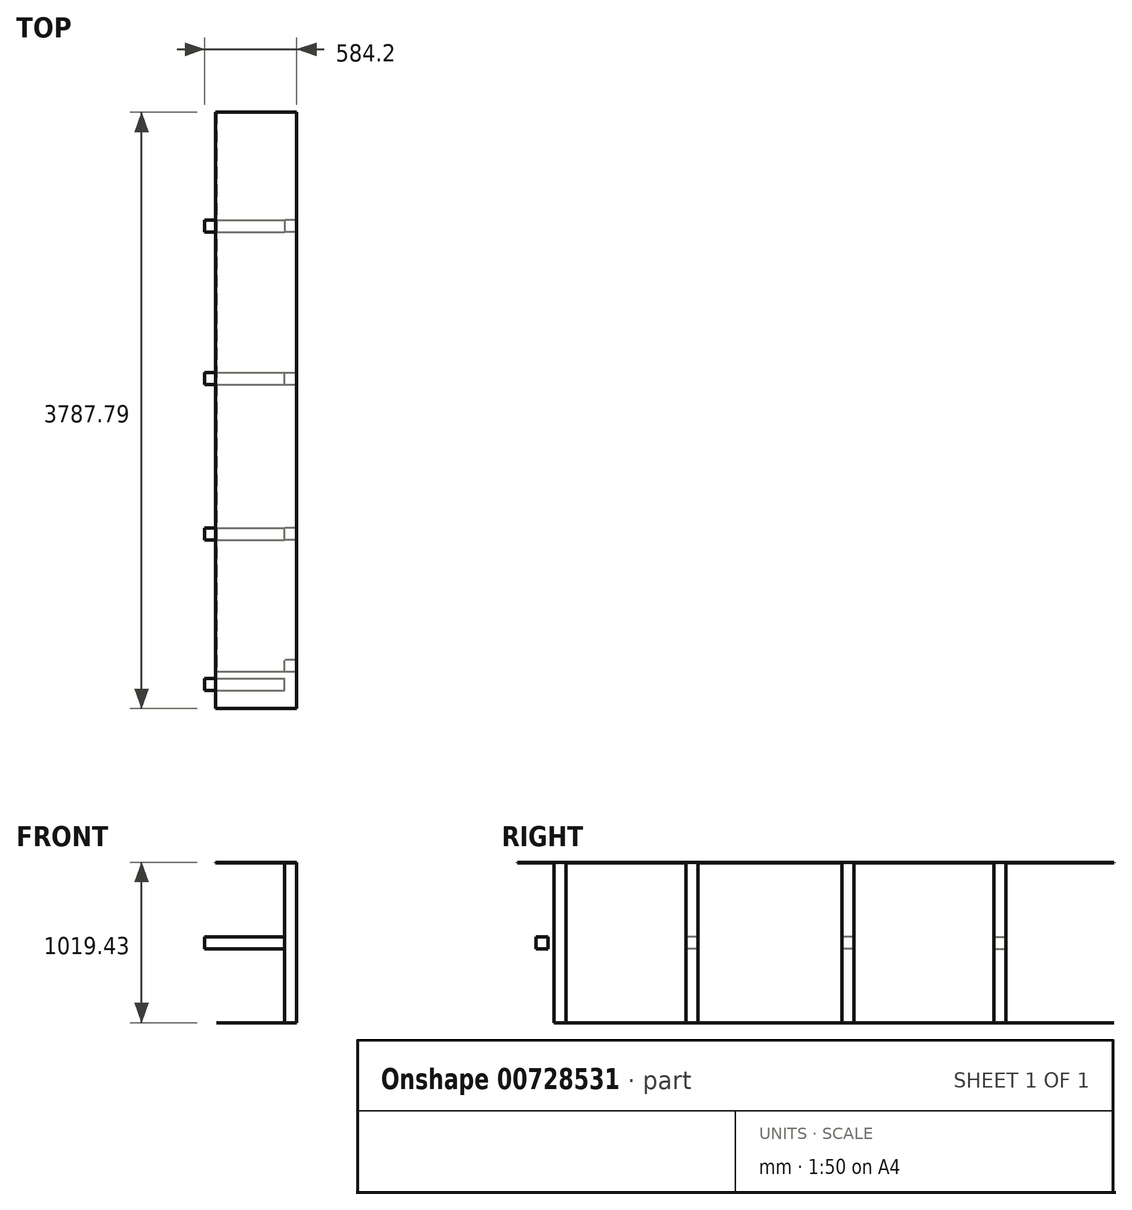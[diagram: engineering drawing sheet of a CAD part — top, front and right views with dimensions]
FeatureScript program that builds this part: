
annotation { "Feature Type Name" : "Feature", "Feature Type Description" : "" }
export const myFeature = defineFeature(function(context is Context, id is Id, definition is map)
    precondition{}
    {
        {
            var Q0;
            Q0=qCreatedBy(makeId("Top.planeOp"),FACE);
            var sketch = newSketch(context, id + "F0", { "sketchPlane" : qUnion([Q0])});
            skLineSegment(sketch, "E0.bottom", {"start": v(254, 1854.2) * mm, "end": v(-254, 1854.2) * mm});
            skLineSegment(sketch, "E0.top", {"start": v(254, -1854.2) * mm, "end": v(-254, -1854.2) * mm});
            skLineSegment(sketch, "E0.left", {"start": v(254, 1854.2) * mm, "end": v(254, -1854.2) * mm});
            skLineSegment(sketch, "E0.right", {"start": v(-254, 1854.2) * mm, "end": v(-254, -1854.2) * mm});
            skPoint(sketch, "E0.middle", {"position": v(0, 0) * mm});
            skLineSegment(sketch, "E1.bottom", {"start": v(254, 1854.2) * mm, "end": v(162.05, 1854.2) * mm});
            skLineSegment(sketch, "E1.left", {"start": v(254, 1854.2) * mm, "end": v(254, 1760.58) * mm});
            skLineSegment(sketch, "E1.right", {"start": v(162.05, 2217.78) * mm, "end": v(162.05, 1854.2) * mm});
            skPoint(sketch, "E2.oppositeSnap0", {"position": v(162.05, 2036) * mm});
            skLineSegment(sketch, "E2.bottom", {"start": v(254, -1854.2) * mm, "end": v(162.05, -1854.2) * mm});
            skLineSegment(sketch, "E2.left", {"start": v(254, -1854.2) * mm, "end": v(254, -1764.17) * mm});
            skLineSegment(sketch, "E2.right", {"start": v(162.05, -1854.2) * mm, "end": v(162.05, -1764.17) * mm});
            skSolve(sketch);
        }
        {
            var Q0;
            Q0 = qSketchRegion(id + "F0", true);
            extrude(context, id + "F1", {"entities" : qUnion([Q0]), "depth" : 0.25 * mm, "offsetDistance" : 25.4 * mm});
        }
        {
            var Q0;
            Q0=makeQuery(id+"F1.opExtrude","CAP_FACE",FACE,{"disambiguationData":[OSD([sQuery(id+"F0.wireOp",EDGE,"E0.bottom"),sQuery(id+"F0.wireOp",EDGE,"E0.top"),sQuery(id+"F0.wireOp",EDGE,"E0.left"),sQuery(id+"F0.wireOp",EDGE,"E0.right"),sQuery(id+"F0.wireOp",EDGE,"E1.bottom"),sQuery(id+"F0.wireOp",EDGE,"E1.left"),sQuery(id+"F0.wireOp",EDGE,"E2.bottom"),sQuery(id+"F0.wireOp",EDGE,"E2.left")])],"isStart":false});
            var sketch = newSketch(context, id + "F2", { "sketchPlane" : qUnion([Q0])});
            skLineSegment(sketch, "E3.bottom", {"start": v(254, 1854.2) * mm, "end": v(177.8, 1854.2) * mm});
            skLineSegment(sketch, "E3.top", {"start": v(254, 1778) * mm, "end": v(177.8, 1778) * mm});
            skLineSegment(sketch, "E3.left", {"start": v(254, 1854.2) * mm, "end": v(254, 1778) * mm});
            skLineSegment(sketch, "E3.right", {"start": v(177.8, 1854.2) * mm, "end": v(177.8, 1778) * mm});
            skLineSegment(sketch, "E4.bottom", {"start": v(254, -1854.2) * mm, "end": v(177.8, -1854.2) * mm});
            skLineSegment(sketch, "E4.top", {"start": v(254, -1778) * mm, "end": v(177.8, -1778) * mm});
            skLineSegment(sketch, "E4.left", {"start": v(254, -1854.2) * mm, "end": v(254, -1778) * mm});
            skLineSegment(sketch, "E4.right", {"start": v(177.8, -1854.2) * mm, "end": v(177.8, -1778) * mm});
            skSolve(sketch);
        }
        {
            var Q0;
            Q0 = qSketchRegion(id + "F2", true);
            extrude(context, id + "F3", {"entities" : qUnion([Q0]), "operationType" : NewBodyOperationType.ADD, "depth" : 1016 * mm, "offsetDistance" : 25.4 * mm});
        }
        {
            var Q0;
            Q0=makeQuery(id+"F3.opExtrude","CAP_FACE",FACE,{"disambiguationData":[OSD([sQuery(id+"F2.wireOp",EDGE,"E3.bottom"),sQuery(id+"F2.wireOp",EDGE,"E3.top"),sQuery(id+"F2.wireOp",EDGE,"E3.left"),sQuery(id+"F2.wireOp",EDGE,"E3.right")])],"isStart":false});
            var sketch = newSketch(context, id + "F4", { "sketchPlane" : qUnion([Q0])});
            skLineSegment(sketch, "E5.bottom", {"start": v(254, 1854.2) * mm, "end": v(-261.64, 1854.2) * mm});
            skLineSegment(sketch, "E5.top", {"start": v(254, -2086) * mm, "end": v(-261.64, -2086) * mm});
            skLineSegment(sketch, "E5.left", {"start": v(254, 1854.2) * mm, "end": v(254, -2086) * mm});
            skLineSegment(sketch, "E5.right", {"start": v(-261.64, 1854.2) * mm, "end": v(-261.64, -2086) * mm});
            skSolve(sketch);
        }
        {
            var Q0;
            Q0 = qSketchRegion(id + "F4", true);
            extrude(context, id + "F5", {"entities" : qUnion([Q0]), "operationType" : NewBodyOperationType.ADD, "depth" : 3.17 * mm, "offsetDistance" : 25.4 * mm});
        }
        {
            var Q0;
            Q0=makeQuery(id+"F3.opExtrude","SWEPT_FACE",FACE,{"disambiguationData":[OSD([sQuery(id+"F2.wireOp",EDGE,"E3.right")])]});
            var sketch = newSketch(context, id + "F6", { "sketchPlane" : qUnion([Q0])});
            skLineSegment(sketch, "E6.bottom", {"start": v(-1778, 546.35) * mm, "end": v(-1854.2, 546.35) * mm});
            skLineSegment(sketch, "E6.top", {"start": v(-1778, 470.15) * mm, "end": v(-1854.2, 470.15) * mm});
            skLineSegment(sketch, "E6.left", {"start": v(-1778, 546.35) * mm, "end": v(-1778, 470.15) * mm});
            skLineSegment(sketch, "E6.right", {"start": v(-1854.2, 546.35) * mm, "end": v(-1854.2, 470.15) * mm});
            skPoint(sketch, "E6.middle", {"position": v(-1816.1, 508.25) * mm});
            skPoint(sketch, "E6.middle.positionSnap0", {"position": v(-1854.2, 508.25) * mm});
            skPoint(sketch, "E6.centerSnap0", {"position": v(-1854.2, 508.25) * mm});
            skSolve(sketch);
        }
        {
            var Q0;
            Q0 = qSketchRegion(id + "F6", true);
            extrude(context, id + "F7", {"entities" : qUnion([Q0]), "operationType" : NewBodyOperationType.ADD, "depth" : 508 * mm, "offsetDistance" : 25.4 * mm});
        }
        {
            var Q0;
            Q0=makeQuery(id+"F3.opExtrude","SWEPT_FACE",FACE,{"disambiguationData":[OSD([sQuery(id+"F2.wireOp",EDGE,"E4.right")])]});
            var sketch = newSketch(context, id + "F8", { "sketchPlane" : qUnion([Q0])});
            skLineSegment(sketch, "E7.bottom", {"start": v(1969.29, 546.1) * mm, "end": v(1893.09, 546.1) * mm});
            skLineSegment(sketch, "E7.top", {"start": v(1969.29, 469.9) * mm, "end": v(1893.09, 469.9) * mm});
            skLineSegment(sketch, "E7.left", {"start": v(1969.29, 546.1) * mm, "end": v(1969.29, 469.9) * mm});
            skLineSegment(sketch, "E7.right", {"start": v(1893.09, 546.1) * mm, "end": v(1893.09, 469.9) * mm});
            skPoint(sketch, "E7.middle", {"position": v(1931.19, 508) * mm});
            skSolve(sketch);
        }
        {
            var Q0;
            Q0 = qSketchRegion(id + "F8", true);
            extrude(context, id + "F9", {"entities" : qUnion([Q0]), "operationType" : NewBodyOperationType.ADD, "depth" : 508 * mm, "offsetDistance" : 25.4 * mm});
        }
        {
            var Q0;
            Q0=makeQuery(id+"F1.opExtrude","CAP_FACE",FACE,{"disambiguationData":[OSD([sQuery(id+"F0.wireOp",EDGE,"E0.bottom"),sQuery(id+"F0.wireOp",EDGE,"E0.top"),sQuery(id+"F0.wireOp",EDGE,"E0.left"),sQuery(id+"F0.wireOp",EDGE,"E0.right"),sQuery(id+"F0.wireOp",EDGE,"E1.bottom"),sQuery(id+"F0.wireOp",EDGE,"E1.left"),sQuery(id+"F0.wireOp",EDGE,"E2.bottom"),sQuery(id+"F0.wireOp",EDGE,"E2.left")])],"isStart":false});
            var sketch = newSketch(context, id + "F10", { "sketchPlane" : qUnion([Q0])});
            skLineSegment(sketch, "E8.bottom", {"start": v(254, 1016) * mm, "end": v(177.8, 1016) * mm});
            skLineSegment(sketch, "E8.top", {"start": v(254, 939.8) * mm, "end": v(177.8, 939.8) * mm});
            skLineSegment(sketch, "E8.left", {"start": v(254, 1016) * mm, "end": v(254, 939.8) * mm});
            skLineSegment(sketch, "E8.right", {"start": v(177.8, 1016) * mm, "end": v(177.8, 939.8) * mm});
            skLineSegment(sketch, "E9.bottom", {"start": v(254, -1016) * mm, "end": v(177.8, -1016) * mm});
            skLineSegment(sketch, "E9.top", {"start": v(254, -939.8) * mm, "end": v(177.8, -939.8) * mm});
            skLineSegment(sketch, "E9.left", {"start": v(254, -1016) * mm, "end": v(254, -939.8) * mm});
            skLineSegment(sketch, "E9.right", {"start": v(177.8, -1016) * mm, "end": v(177.8, -939.8) * mm});
            skLineSegment(sketch, "E10.bottom", {"start": v(177.8, -26.4) * mm, "end": v(254, -26.4) * mm});
            skLineSegment(sketch, "E10.top", {"start": v(177.8, 49.8) * mm, "end": v(254, 49.8) * mm});
            skLineSegment(sketch, "E10.left", {"start": v(177.8, -26.4) * mm, "end": v(177.8, 49.8) * mm});
            skLineSegment(sketch, "E10.right", {"start": v(254, -26.4) * mm, "end": v(254, 49.8) * mm});
            skPoint(sketch, "E10.middle", {"position": v(215.9, 11.7) * mm});
            skSolve(sketch);
        }
        {
            var Q0;
            Q0 = qSketchRegion(id + "F10", true);
            extrude(context, id + "F11", {"entities" : qUnion([Q0]), "operationType" : NewBodyOperationType.ADD, "depth" : 1016 * mm, "offsetDistance" : 25.4 * mm});
        }
        {
            var Q0;
            Q0=makeQuery(id+"F11.opExtrude","SWEPT_FACE",FACE,{"disambiguationData":[OSD([sQuery(id+"F10.wireOp",EDGE,"E8.right")])]});
            var sketch = newSketch(context, id + "F12", { "sketchPlane" : qUnion([Q0])});
            skLineSegment(sketch, "E11.bottom", {"start": v(-939.8, 546.35) * mm, "end": v(-1016, 546.35) * mm});
            skLineSegment(sketch, "E11.top", {"start": v(-939.8, 470.15) * mm, "end": v(-1016, 470.15) * mm});
            skLineSegment(sketch, "E11.left", {"start": v(-939.8, 546.35) * mm, "end": v(-939.8, 470.15) * mm});
            skLineSegment(sketch, "E11.right", {"start": v(-1016, 546.35) * mm, "end": v(-1016, 470.15) * mm});
            skPoint(sketch, "E11.middle", {"position": v(-977.9, 508.25) * mm});
            skPoint(sketch, "E11.middle.positionSnap0", {"position": v(-1016, 508.25) * mm});
            skPoint(sketch, "E11.centerSnap0", {"position": v(-1016, 508.25) * mm});
            skSolve(sketch);
        }
        {
            var Q0;
            Q0 = qSketchRegion(id + "F12", true);
            extrude(context, id + "F13", {"entities" : qUnion([Q0]), "operationType" : NewBodyOperationType.ADD, "depth" : 508 * mm, "offsetDistance" : 25.4 * mm});
        }
        {
            var Q0;
            Q0=makeQuery(id+"F11.opExtrude","SWEPT_FACE",FACE,{"disambiguationData":[OSD([sQuery(id+"F10.wireOp",EDGE,"E10.left")])]});
            var sketch = newSketch(context, id + "F14", { "sketchPlane" : qUnion([Q0])});
            skLineSegment(sketch, "E12.bottom", {"start": v(-49.8, 546.1) * mm, "end": v(26.4, 546.1) * mm});
            skLineSegment(sketch, "E12.top", {"start": v(-49.8, 469.9) * mm, "end": v(26.4, 469.9) * mm});
            skLineSegment(sketch, "E12.left", {"start": v(-49.8, 546.1) * mm, "end": v(-49.8, 469.9) * mm});
            skLineSegment(sketch, "E12.right", {"start": v(26.4, 546.1) * mm, "end": v(26.4, 469.9) * mm});
            skSolve(sketch);
        }
        {
            var Q0;
            Q0 = qSketchRegion(id + "F14", true);
            extrude(context, id + "F15", {"entities" : qUnion([Q0]), "operationType" : NewBodyOperationType.ADD, "depth" : 508 * mm, "offsetDistance" : 25.4 * mm});
        }
        {
            var Q0;
            Q0=makeQuery(id+"F11.opExtrude","SWEPT_FACE",FACE,{"disambiguationData":[OSD([sQuery(id+"F10.wireOp",EDGE,"E9.right")])]});
            var sketch = newSketch(context, id + "F16", { "sketchPlane" : qUnion([Q0])});
            skLineSegment(sketch, "E13.bottom", {"start": v(939.8, 546.1) * mm, "end": v(1016, 546.1) * mm});
            skLineSegment(sketch, "E13.top", {"start": v(939.8, 469.9) * mm, "end": v(1016, 469.9) * mm});
            skLineSegment(sketch, "E13.left", {"start": v(939.8, 546.1) * mm, "end": v(939.8, 469.9) * mm});
            skLineSegment(sketch, "E13.right", {"start": v(1016, 546.1) * mm, "end": v(1016, 469.9) * mm});
            skSolve(sketch);
        }
        {
            var Q0;
            Q0 = qSketchRegion(id + "F16", true);
            extrude(context, id + "F17", {"entities" : qUnion([Q0]), "operationType" : NewBodyOperationType.ADD, "depth" : 508 * mm, "offsetDistance" : 25.4 * mm});
        }
        {
            var Q0;
            Q0=makeQuery(id+"F5.opExtrude","CAP_FACE",FACE,{"disambiguationData":[OSD([sQuery(id+"F4.wireOp",EDGE,"E5.bottom"),sQuery(id+"F4.wireOp",EDGE,"E5.top"),sQuery(id+"F4.wireOp",EDGE,"E5.left"),sQuery(id+"F4.wireOp",EDGE,"E5.right")])],"isStart":false});
            var sketch = newSketch(context, id + "F18", { "sketchPlane" : qUnion([Q0])});
            skLineSegment(sketch, "E14.bottom", {"start": v(254, 1854.2) * mm, "end": v(-893.8, 1854.2) * mm});
            skLineSegment(sketch, "E14.top", {"start": v(254, 1701.8) * mm, "end": v(-893.8, 1701.8) * mm});
            skLineSegment(sketch, "E14.left", {"start": v(254, 1854.2) * mm, "end": v(254, 1701.8) * mm});
            skLineSegment(sketch, "E14.right", {"start": v(-893.8, 1854.2) * mm, "end": v(-893.8, 1701.8) * mm});
            skSolve(sketch);
        }
        {
            var Q0;
            Q0 = qSketchRegion(id + "F18", true);
            extrude(context, id + "F19", {"entities" : qUnion([Q0]), "operationType" : NewBodyOperationType.REMOVE, "endBound" : BoundingType.THROUGH_ALL, "oppositeDirection" : true, "depth" : 25.4 * mm, "offsetDistance" : 25.4 * mm});
        }
    });
